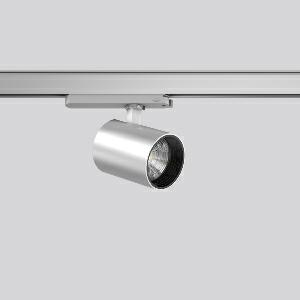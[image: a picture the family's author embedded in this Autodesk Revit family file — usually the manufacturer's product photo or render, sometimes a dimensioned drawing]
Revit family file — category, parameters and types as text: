
# Revit family: deecos_s_mini_track-in_742263_004_22c2
name_source: partatom
category: Lighting Fixtures
units: mm (PartAtom-declared; Revit-internal decimal feet)

## family parameters
Cut with Voids When Loaded = No
Host = Face
Light Source = No
Part Type = Normal
Room Calculation Point = No
Round Connector Dimension = Use Diameter
Shared = No

## types (1)
- DEECOS S mini track-in (1 x LED Modul 930, 2850 lm, 3000)
    Apparent Load = 29 VA
    Approval mark = CE
    CIE Flux Codes = 98 100 100 100 100
    Color Rendering = 90
    Color Temperature = 3000
    Default Elevation = 1800 mm
    Description = Series: DEECOS S mini track-in
LED surface-mounted projector in modern design with no visible cooling ribs. Housing: die-cast aluminium, powder-coated. Rotation range: 356°. Swivel range: 90°. Black plastic ring and recessed LED to prevent glare from the side. Optical assembly with lens made of plastic (polycarbonate) for the best homogeneous light distribution - can be changed without tools. Best colour rendering index Ra>90. With multi adaptor for 3-circuit tracks 230 V. Suitable for Track on ceiling, Wall track. Track-in driver integrated into the adapter. High quality converter without flickering and stroboscopic effect. The following accessories can be mounted without use of tools: interchangeable lenses, decorative glasses, honeycomb louvre, clear and frosted diffusers, white interchangeable plastic ring. 
Colour: silver
Diameter: 87 mm
Height: 135 mm
Lamp: LED
Socket: without socket
Colour temperature: 3000K
Colour rendering index (CRI): 92
System power: 29 W
Rated luminous flux: 2850 lm
Luminous efficiency: 98 lm/W
Control gear: Regulated power supply
Protection class: II
Type of protection: IP 20
    Height = 135 mm
    Lamp = 1 x LED Modul 930
    Lamp Light Flux = 2850 lm
    Lamp count = 1
    Length = 87 mm
    Lifetime = 50000 h
    Luminous efficacy = 98 lm/W
    Manufacturer = RZB
    ModVariant = No
    Model = 742263.004
    Mounting Place = Ceiling
    Mounting Type = Rail mounted
    Number of Poles = 1
    OnlyDefault = Yes
    Power Factor = 1
    Product Name = DEECOS S mini track-in
    Product group = Track mounted projectors
    ProductGroupID = 301
    Protection Class = Protection class II
    Protection Degree = IP 20
    RLX_Detail_Level = 1
    RLX_Emergency_Light_Flux = 0 lm
    RLX_Emergency_Type = 0
    RLX_Emergency_Type_DB = No
    RlxData = <blob elided: 35793 chars, md5=c4525fd9>
    Socket = socket
    Standby Power = 0 W
    System Light Flux = 2850 lm
    System Power = 29 W
    Type Comments = Product without accessories
    Type Image = 742102.004.jpg
    URL = http://relux.com
    VarID = ---
    Voltage = 230 V
    Voltage Range = 220-240 V
    Weight = 0.00 kg
    Width = 0 mm  [stored 0 ft]

note: [stored X ft] marks values corroborated as IEEE doubles in the binary element streams (Revit-internal decimal feet)

## geometry (parser evidence)
native form markers: Blend x4, Sweep x12
no freeform markers — native parametric forms only
